# Revit family: Urinal-High_Efficiency-Whitehall-BestCare-WH2158W-SLPT-EB
name_source: partatom
category: Plumbing Fixtures
units: mm (PartAtom-declared; Revit-internal decimal feet)

## family parameters
Cut with Voids When Loaded = No
Host = Face
OmniClass Number = 23.45.05.21.11.21
OmniClass Title = Urinals
Part Type = Normal
Room Calculation Point = No
Round Connector Dimension = Use Diameter
Shared = Yes

## types (1)
- WH2158W-SLPT-EB
    Assembly Code = D2010210
    CW Connection = No
    CWFU = 5
    Default Elevation = 20"
    Description = BestCare® Ligature-Resistant Urinal, High Efficiency, Wall Supply
    Finish = Stainless Steel-Whitehall-Powder Coated White
    Flush Rate = 0.125 GPF (0.47 LPF) to 0.5 GPF (1.8 LPF)
    HW Connection = No
    HWFU = 0
    Height = 24"
    Inlet Connection Diameter = 3/4"
    Installation Type = Wall Mounted
    Length = 14 1/2"
    Manufacturer = Whitehall Manufacturing
    Material = Stainless Steel-Whitehall-Powder Coated White
    Model = WH2158W-SLPT-EB
    Product Documentation Link = https://www.whitehallmfg.com
    Product Page URL = https://www.whitehallmfg.com
    URL = https://www.whitehallmfg.com
    Vent Connection = No
    WFU = 5
    WH2898-ADA-EG10-0.125 Access Panel with Hydraulic Flush Valve for Urinal, 0.125 GPF (White) = No
    WH2898-ADA-EG10-0.5 Access Panel with Hydraulic Flush Valve for Urinal, 0.5 GPF (White) = No
    Waste Connection = Yes
    Waste Connection Diameter = 1 1/2"
    Waste Connection Height = 14 1/2"
    Waste Connection Radius = 3/4"
    Width = 13"

## geometry (parser evidence)
native form markers: Sweep x3
no freeform markers — native parametric forms only
